# Revit family: BuzziSpace - BuzziShade
name_source: partatom
category: Lighting Fixtures
units: mm (PartAtom-declared; Revit-internal decimal feet)

## family parameters
Always vertical = Yes
Cut with Voids When Loaded = No
Host = Ceiling
Light Source = No
OmniClass Number = 23.80.70.11
OmniClass Title = Luminaries for Internal Lighting
Part Type = Normal
Room Calculation Point = No
Round Connector Dimension = Use Diameter
Shared = No

## types (10) — shared parameters
Manufacturer = BuzziSpace

## per-type parameters (varying)
| type | Diffuser | Electrification | Glass | Globe | L | M | M + L Cables | Model | Reflector | Retrofit | Spot | XL | XXL |
| XL- LED Disk | <By Category> | Yes | <By Category> | No | No | No | No | BuzziShade XL - LED Disk | <By Category> | No | No | Yes | No |
| XL - No Electrification | <By Category> | No | <By Category> | No | No | No | No | BuzziShade XL - No Electrification | <By Category> | No | No | Yes | No |
| XXL- LED Disk | <By Category> | Yes | <By Category> | No | No | No | No | BuzziShade XXL - LED Disk | Diffuser | No | No | No | Yes |
| XXL- No Electrification | <By Category> | No | <By Category> | No | No | No | No | BuzziShade XXL - No Electrification | Diffuser | No | No | No | Yes |
| Large - Sol Solo Globe | Diffuser | Yes | Glass | Yes | Yes | No | Yes | BuzziShade Large - Sol Solo Globe | Reflector | No | No | No | No |
| Large - Sol Solo Spot | <By Category> | Yes | <By Category> | No | Yes | No | Yes | BuzziShade Large - Sol Solo Spot | Diffuser | No | Yes | No | No |
| Medium - Sol Solo Globe | <By Category> | Yes | <By Category> | Yes | No | Yes | Yes | BuzziShade Medium - Sol Solo Globe | Diffuser | Yes | No | No | No |
| Medium - Sol Solo Spot | <By Category> | Yes | <By Category> | No | No | Yes | Yes | BuzziShade Medium - Sol Solo Spot | Diffuser | No | Yes | No | No |
| Medium - Retrofit | <By Category> | Yes | <By Category> | No | No | Yes | Yes | BuzziShade Medium - Sol Solo Retrofit | Diffuser | Yes | No | No | No |
| Large- Retrofit | <By Category> | Yes | <By Category> | No | Yes | No | Yes | BuzziShade Large - Sol Solo Retrofit | Diffuser | Yes | No | No | No |

## geometry (parser evidence)
native form markers: Sweep x9
no freeform markers — native parametric forms only
